annotation { "Feature Type Name" : "Feature", "Feature Type Description" : "" }
export const myFeature = defineFeature(function(context is Context, id is Id, definition is map)
    precondition{}
    {
        {
            var Q0;
            Q0=qCreatedBy(makeId("Top.planeOp"),FACE);
            var sketch = newSketch(context, id + "F0", { "sketchPlane" : qUnion([Q0])});
            skLineSegment(sketch, "E0.bottom", {"start": v(0.13, 0) * mm, "end": v(85.6, 0) * mm});
            skLineSegment(sketch, "E0.top", {"start": v(0.13, 53.97) * mm, "end": v(85.6, 53.97) * mm});
            skLineSegment(sketch, "E0.left", {"start": v(0, 0.13) * mm, "end": v(0, 53.85) * mm});
            skLineSegment(sketch, "E0.right", {"start": v(85.73, 0.13) * mm, "end": v(85.73, 53.85) * mm});
            skText(sketch, "E1", { "text": "Evan Mensinger\nMechanical Engineer\<email>", "fontName": "AllertaStencil-Regular.ttf"});
            skPoint(sketch, "E2.visualSharp", {"position": v(0, 53.97) * mm});
            skArc(sketch, "E2.filletArc", {"start": v(0.13, 53.97) * mm, "mid": v(0.04, 53.94) * mm, "end": v(0, 53.85) * mm});
            skPoint(sketch, "E3.visualSharp", {"position": v(85.73, 53.97) * mm});
            skArc(sketch, "E3.filletArc", {"start": v(85.73, 53.85) * mm, "mid": v(85.69, 53.94) * mm, "end": v(85.6, 53.97) * mm});
            skPoint(sketch, "E4.visualSharp", {"position": v(85.73, 0) * mm});
            skArc(sketch, "E4.filletArc", {"start": v(85.6, 0) * mm, "mid": v(85.69, 0.04) * mm, "end": v(85.73, 0.13) * mm});
            skPoint(sketch, "E5.visualSharp", {"position": v(0, 0) * mm});
            skArc(sketch, "E5.filletArc", {"start": v(0, 0.13) * mm, "mid": v(0.04, 0.04) * mm, "end": v(0.13, 0) * mm});
            skLineSegment(sketch, "E6", {"start": v(3.18, 30.91) * mm, "end": v(3.18, 35.63) * mm, "construction": true});
            skLineSegment(sketch, "E7", {"start": v(7.43, 50.8) * mm, "end": v(13.66, 50.8) * mm, "construction": true});
            skArc(sketch, "E8", {"start": v(7.43, 50.8) * mm, "mid": v(15.32, 44.96) * mm, "end": v(23.68, 39.82) * mm});
            skArc(sketch, "E9", {"start": v(13.66, 50.8) * mm, "mid": v(22.37, 44.99) * mm, "end": v(31.58, 40.02) * mm});
            skArc(sketch, "E10", {"start": v(19.47, 36.18) * mm, "mid": v(10.82, 35.1) * mm, "end": v(3.18, 30.91) * mm});
            skArc(sketch, "E11", {"start": v(19.7, 39.98) * mm, "mid": v(11.1, 39.14) * mm, "end": v(3.17, 35.63) * mm});
            skArc(sketch, "E12", {"start": v(19.47, 36.18) * mm, "mid": v(36.15, 36.62) * mm, "end": v(52.49, 39.98) * mm});
            skArc(sketch, "E13", {"start": v(19.7, 39.98) * mm, "mid": v(23.68, 39.82) * mm, "end": v(27.66, 39.84) * mm});
            skLineSegment(sketch, "E14", {"start": v(7.43, 50.8) * mm, "end": v(3.17, 50.8) * mm});
            skLineSegment(sketch, "E15", {"start": v(3.17, 50.8) * mm, "end": v(3.18, 35.63) * mm});
            skLineSegment(sketch, "E16", {"start": v(13.66, 50.8) * mm, "end": v(61.6, 50.8) * mm});
            skLineSegment(sketch, "E17", {"start": v(3.18, 30.91) * mm, "end": v(3.18, 28.37) * mm});
            skLineSegment(sketch, "E18", {"start": v(3.18, 28.37) * mm, "end": v(82.55, 28.37) * mm});
            skLineSegment(sketch, "E19", {"start": v(82.55, 28.37) * mm, "end": v(82.55, 39.25) * mm});
            skArc(sketch, "E20", {"start": v(61.6, 50.8) * mm, "mid": v(70.79, 42.7) * mm, "end": v(82.55, 39.25) * mm});
            skArc(sketch, "E21", {"start": v(66.52, 50.8) * mm, "mid": v(73.8, 45.42) * mm, "end": v(82.55, 43.07) * mm});
            skLineSegment(sketch, "E22", {"start": v(66.52, 50.8) * mm, "end": v(75.56, 50.8) * mm});
            skLineSegment(sketch, "E23", {"start": v(82.55, 50.8) * mm, "end": v(82.55, 43.07) * mm});
            skArc(sketch, "E24", {"start": v(52.49, 39.98) * mm, "mid": v(65.46, 44.68) * mm, "end": v(77.82, 50.8) * mm});
            skArc(sketch, "E25", {"start": v(27.66, 39.84) * mm, "mid": v(52.16, 42.93) * mm, "end": v(75.56, 50.8) * mm});
            skPoint(sketch, "E26", {"position": v(74.54, 50.8) * mm});
            skArc(sketch, "E27", {"start": v(23.68, 39.82) * mm, "mid": v(45.51, 32.9) * mm, "end": v(68.3, 35.11) * mm});
            skArc(sketch, "E28", {"start": v(31.58, 40.02) * mm, "mid": v(49.55, 34.66) * mm, "end": v(68.3, 35.11) * mm});
            skLineSegment(sketch, "E29.trimOffspring", {"start": v(77.82, 50.8) * mm, "end": v(82.55, 50.8) * mm});
            skArc(sketch, "E30", {"start": v(76.94, 11.84) * mm, "mid": v(72.2, 23.94) * mm, "end": v(59.43, 21.47) * mm});
            skArc(sketch, "E31", {"start": v(76.94, 11.84) * mm, "mid": v(70.47, 20.81) * mm, "end": v(59.43, 21.47) * mm});
            skLineSegment(sketch, "E32", {"start": v(72.2, 23.94) * mm, "end": v(64.25, 9.51) * mm, "construction": true});
            const initialGuessF0  = {"E1": [0.00317, 0.02064, 1, 0, 0.00456]};
            skSetInitialGuess(sketch, initialGuessF0);
            skSolve(sketch);
        }
        {
            var Q0;
            Q0 = qSketchRegion(id + "F0", true);
            var Q1;
            {var subQ5=sQuery(id+"F0.wireOp",EDGE,"E24");var subQ7=sQuery(id+"F0.wireOp",EDGE,"E12");var subQ8=makeQuery(id+"F0.imprint","INTERSECT",VERTEX,{"derivedFrom":[subQ7,subQ5]});Q1=makeQuery(id+"F0.imprint","IMPRINT",FACE,{"disambiguationData":[TD([[makeQuery(id+"F0.imprint","IMPRINT",EDGE,{"disambiguationData":[TD([[subQ8,1.0]])],"derivedFrom":subQ7}),1.0]])]});}
            var Q2;
            {var subQ5=sQuery(id+"F0.wireOp",EDGE,"E27");var subQ7=sQuery(id+"F0.wireOp",EDGE,"E12");var subQ8=makeQuery(id+"F0.imprint","INTERSECT",VERTEX,{"derivedFrom":[subQ7,subQ5]});Q2=makeQuery(id+"F0.imprint","IMPRINT",FACE,{"disambiguationData":[TD([[makeQuery(id+"F0.imprint","IMPRINT",EDGE,{"disambiguationData":[TD([[subQ8,-1.0]])],"derivedFrom":subQ7}),1.0]])]});}
            var Q3;
            {var subQ0=sQuery(id+"F0.wireOp",EDGE,"E27");var subQ1=sQuery(id+"F0.wireOp",EDGE,"E12");var subQ2=makeQuery(id+"F0.imprint","INTERSECT",VERTEX,{"derivedFrom":[subQ1,subQ0]});Q3=makeQuery(id+"F0.imprint","IMPRINT",FACE,{"disambiguationData":[TD([[makeQuery(id+"F0.imprint","IMPRINT",EDGE,{"disambiguationData":[TD([[subQ2,-1.0]])],"derivedFrom":subQ1}),-1.0]])]});}
            var Q4;
            {var subQ0=sQuery(id+"F0.wireOp",EDGE,"E25");var subQ1=sQuery(id+"F0.wireOp",EDGE,"E20");var subQ2=makeQuery(id+"F0.imprint","INTERSECT",VERTEX,{"derivedFrom":[subQ1,subQ0]});Q4=makeQuery(id+"F0.imprint","IMPRINT",FACE,{"disambiguationData":[TD([[makeQuery(id+"F0.imprint","IMPRINT",EDGE,{"disambiguationData":[TD([[subQ2,-1.0]])],"derivedFrom":subQ1}),1.0]])]});}
            extrude(context, id + "F1", {"entities" : qUnion([Q0, Q1, Q2, Q3, Q4]), "depth" : 0.5 * mm, "offsetDistance" : 25.4 * mm});
        }
    });